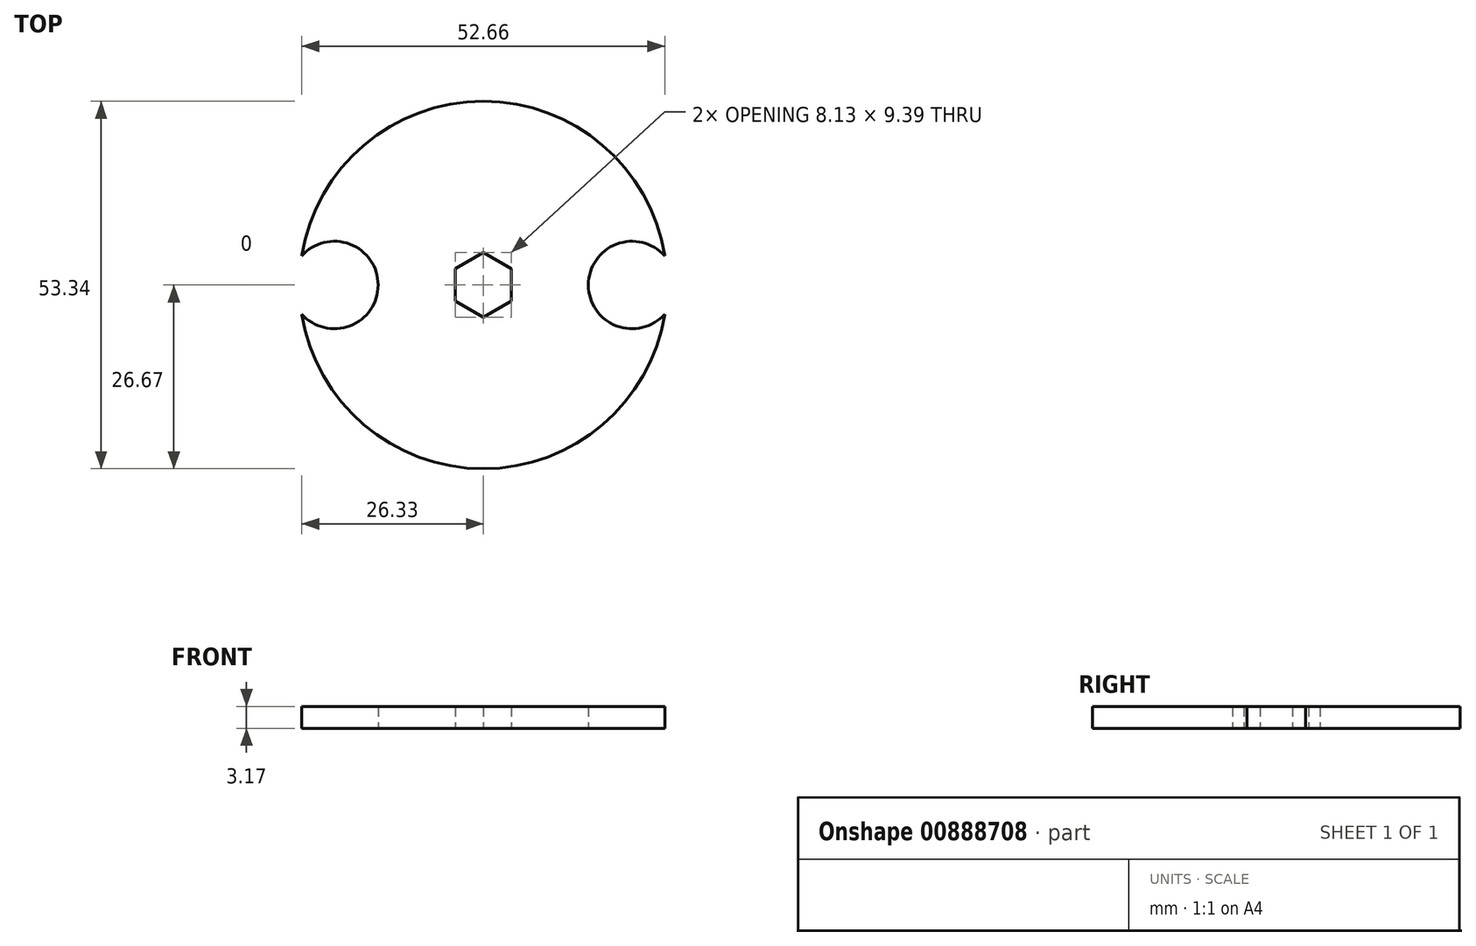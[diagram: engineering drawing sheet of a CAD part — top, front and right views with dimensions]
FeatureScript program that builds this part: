
annotation { "Feature Type Name" : "Feature", "Feature Type Description" : "" }
export const myFeature = defineFeature(function(context is Context, id is Id, definition is map)
    precondition{}
    {
        {
            var Q0;
            Q0=qCreatedBy(makeId("Top.planeOp"),FACE);
            var sketch = newSketch(context, id + "F0", { "sketchPlane" : qUnion([Q0])});
            skLineSegment(sketch, "E0.0", {"start": v(4.06, 2.35) * mm, "end": v(4.06, -2.35) * mm});
            skLineSegment(sketch, "E0.1", {"start": v(4.06, -2.35) * mm, "end": v(0, -4.7) * mm});
            skLineSegment(sketch, "E0.2", {"start": v(0, -4.7) * mm, "end": v(-4.06, -2.35) * mm});
            skLineSegment(sketch, "E0.3", {"start": v(-4.06, -2.35) * mm, "end": v(-4.06, 2.35) * mm});
            skLineSegment(sketch, "E0.4", {"start": v(-4.06, 2.35) * mm, "end": v(0, 4.7) * mm});
            skLineSegment(sketch, "E0.5", {"start": v(0, 4.7) * mm, "end": v(4.06, 2.35) * mm});
            skPoint(sketch, "E0.0.midPoint", {"position": v(4.06, 0) * mm});
            skArc(sketch, "E1", {"start": v(-26.33, -4.24) * mm, "mid": v(0, -26.67) * mm, "end": v(26.33, -4.24) * mm});
            skLineSegment(sketch, "E2", {"start": v(0, 4.7) * mm, "end": v(0, -4.7) * mm, "construction": true});
            skLineSegment(sketch, "E3", {"start": v(0, 0) * mm, "end": v(-26.67, 0.03) * mm, "construction": true});
            skLineSegment(sketch, "E4", {"start": v(-21.6, 0) * mm, "end": v(-21.57, -10.51) * mm, "construction": true});
            skPoint(sketch, "E5.0.midPoint", {"position": v(-17.25, -2.43) * mm});
            skArc(sketch, "E6.cCircle", {"start": v(-26.33, -4.24) * mm, "mid": v(-15.25, 0) * mm, "end": v(-26.33, 4.24) * mm});
            skArc(sketch, "E7", {"start": v(26.33, 4.24) * mm, "mid": v(15.25, 0) * mm, "end": v(26.33, -4.24) * mm});
            skArc(sketch, "E8.trimOffspring", {"start": v(26.33, 4.24) * mm, "mid": v(0, 26.67) * mm, "end": v(-26.33, 4.24) * mm});
            skArc(sketch, "E9.trimOffspring", {"start": v(-4.06, 0) * mm, "mid": v(-4.06, 0) * mm, "end": v(-4.06, 0) * mm, "construction": true});
            skSolve(sketch);
        }
        {
            var Q0;
            Q0 = qSketchRegion(id + "F0", true);
            extrude(context, id + "F1", {"entities" : qUnion([Q0]), "depth" : 3.17 * mm, "offsetDistance" : 25 * mm});
        }
    });
